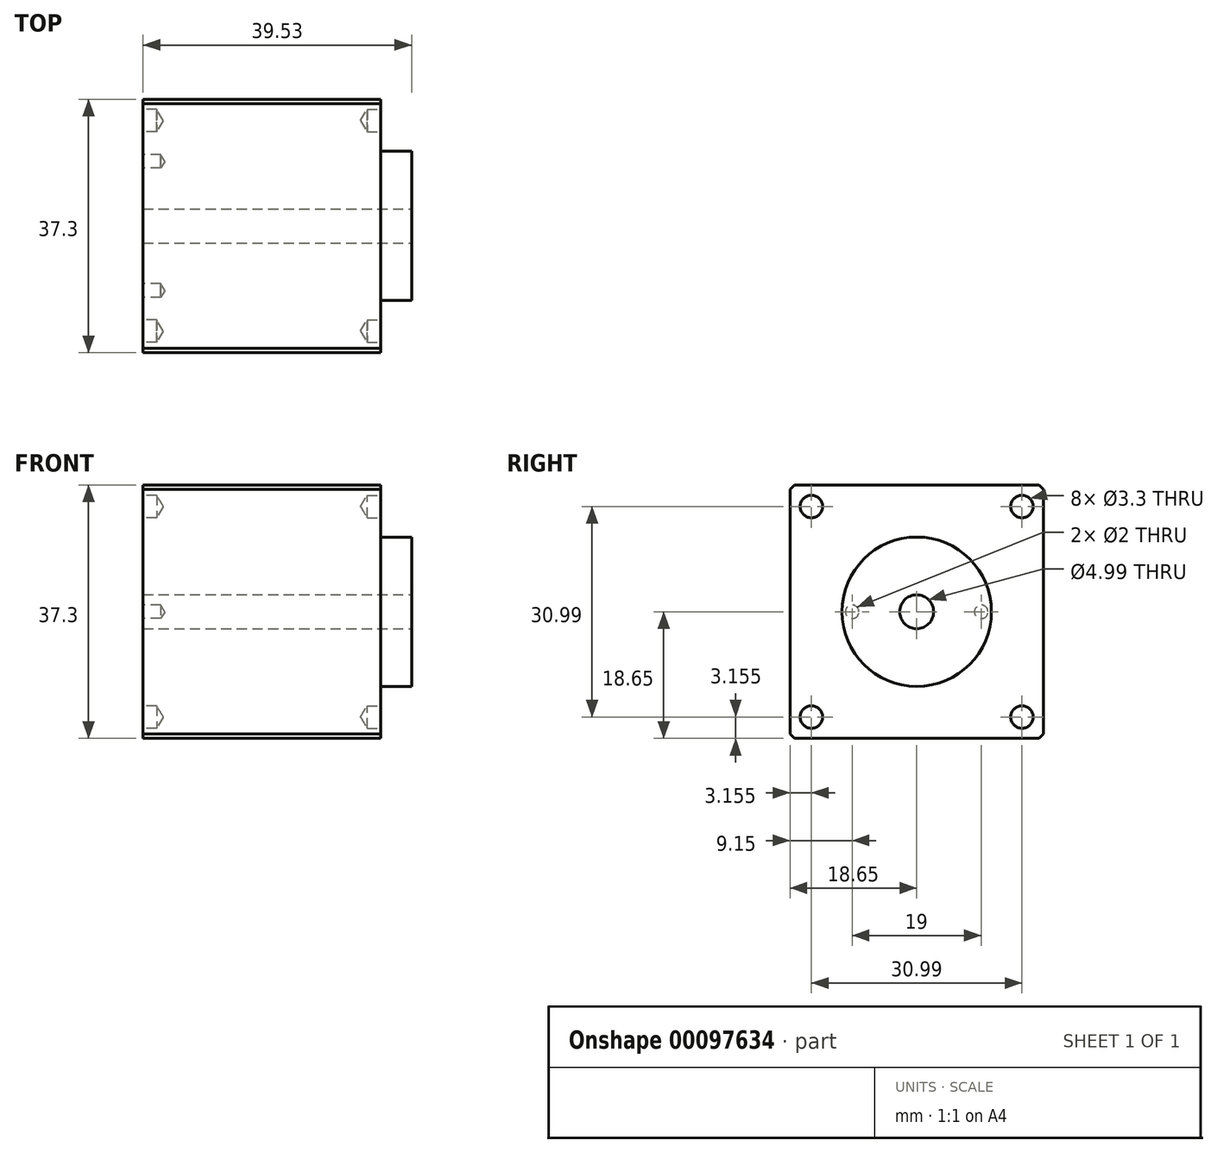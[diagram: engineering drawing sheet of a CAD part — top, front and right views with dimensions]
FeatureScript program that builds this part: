
annotation { "Feature Type Name" : "Feature", "Feature Type Description" : "" }
export const myFeature = defineFeature(function(context is Context, id is Id, definition is map)
    precondition{}
    {
        {
            var Q0;
            Q0=qCreatedBy(makeId("Right.planeOp"),FACE);
            var sketch = newSketch(context, id + "F0", { "sketchPlane" : qUnion([Q0])});
            skLineSegment(sketch, "E0.bottom", {"start": v(18, -18.65) * mm, "end": v(-18, -18.65) * mm});
            skLineSegment(sketch, "E0.top", {"start": v(18, 18.65) * mm, "end": v(-18, 18.65) * mm});
            skLineSegment(sketch, "E0.left", {"start": v(18.65, -18) * mm, "end": v(18.65, 18) * mm});
            skLineSegment(sketch, "E0.right", {"start": v(-18.65, -18) * mm, "end": v(-18.65, 18) * mm});
            skPoint(sketch, "E0.middle", {"position": v(0, 0) * mm});
            skLineSegment(sketch, "E1", {"start": v(-18, 18.65) * mm, "end": v(-18.65, 18) * mm});
            skLineSegment(sketch, "E2.MirrorCS", {"start": v(18, 18.65) * mm, "end": v(18.65, 18) * mm});
            skLineSegment(sketch, "E3.MirrorCS", {"start": v(-18, -18.65) * mm, "end": v(-18.65, -18) * mm});
            skLineSegment(sketch, "E4.MirrorCS", {"start": v(18, -18.65) * mm, "end": v(18.65, -18) * mm});
            skCircle(sketch, "E5", {"center": v(0, 0) * mm, "radius": 11 * mm});
            skCircle(sketch, "E6", {"center": v(0, 0) * mm, "radius": 2.5 * mm});
            skPoint(sketch, "E7", {"position": v(-15.5, 15.5) * mm});
            skPoint(sketch, "E8.MirrorP", {"position": v(15.5, 15.5) * mm});
            skPoint(sketch, "E9.MirrorP", {"position": v(-15.5, -15.5) * mm});
            skPoint(sketch, "E10.MirrorP", {"position": v(15.5, -15.5) * mm});
            skPoint(sketch, "E11", {"position": v(-9.5, 0) * mm});
            skPoint(sketch, "E12.MirrorP", {"position": v(9.5, 0) * mm});
            skSolve(sketch);
        }
        {
            var Q0;
            Q0=makeQuery(id+"F0.imprint","IMPRINT",FACE,{"disambiguationData":[TD([[makeQuery(id+"F0.imprint","IMPRINT",EDGE,{"derivedFrom":sQuery(id+"F0.wireOp",EDGE,"E0.bottom")}),-1.0]])]});
            extrude(context, id + "F1", {"entities" : qUnion([Q0]), "endBound" : BoundingType.SYMMETRIC, "depth" : 35 * mm});
        }
        {
            var Q0;
            Q0=makeQuery(id+"F0.imprint","IMPRINT",FACE,{"disambiguationData":[TD([[makeQuery(id+"F0.imprint","IMPRINT",EDGE,{"derivedFrom":sQuery(id+"F0.wireOp",EDGE,"E5")}),1.0]])]});
            var Q1;
            Q1=makeQuery(id+"F1.opExtrude","CAP_FACE",FACE,{"disambiguationData":[OSD([sQuery(id+"F0.wireOp",EDGE,"E0.bottom"),sQuery(id+"F0.wireOp",EDGE,"E0.top"),sQuery(id+"F0.wireOp",EDGE,"E0.left"),sQuery(id+"F0.wireOp",EDGE,"E0.right"),sQuery(id+"F0.wireOp",EDGE,"E1"),sQuery(id+"F0.wireOp",EDGE,"E2.MirrorCS"),sQuery(id+"F0.wireOp",EDGE,"E3.MirrorCS"),sQuery(id+"F0.wireOp",EDGE,"E4.MirrorCS"),sQuery(id+"F0.wireOp",EDGE,"E5")])],"isStart":true});
            extrude(context, id + "F2", {"entities" : qUnion([Q0]), "operationType" : NewBodyOperationType.ADD, "endBound" : BoundingType.UP_TO_SURFACE, "oppositeDirection" : true, "endBoundEntityFace" : qUnion([Q1]), "depth" : 15 * mm});
        }
        {
            var Q0;
            Q0=makeQuery(id+"F0.imprint","IMPRINT",FACE,{"disambiguationData":[TD([[makeQuery(id+"F0.imprint","IMPRINT",EDGE,{"derivedFrom":sQuery(id+"F0.wireOp",EDGE,"E5")}),1.0]])]});
            extrude(context, id + "F3", {"entities" : qUnion([Q0]), "operationType" : NewBodyOperationType.ADD, "depth" : 22.03 * mm});
        }
        {
            var Q0;
            Q0=makeQuery(id+"F1.opExtrude","CAP_FACE",FACE,{"disambiguationData":[OSD([sQuery(id+"F0.wireOp",EDGE,"E0.bottom"),sQuery(id+"F0.wireOp",EDGE,"E0.top"),sQuery(id+"F0.wireOp",EDGE,"E0.left"),sQuery(id+"F0.wireOp",EDGE,"E0.right"),sQuery(id+"F0.wireOp",EDGE,"E1"),sQuery(id+"F0.wireOp",EDGE,"E2.MirrorCS"),sQuery(id+"F0.wireOp",EDGE,"E3.MirrorCS"),sQuery(id+"F0.wireOp",EDGE,"E4.MirrorCS"),sQuery(id+"F0.wireOp",EDGE,"E5")])],"isStart":false});
            var sketch = newSketch(context, id + "F4", { "sketchPlane" : qUnion([Q0])});
            skPoint(sketch, "E13", {"position": v(-15.5, 15.5) * mm});
            skPoint(sketch, "E14", {"position": v(-15.5, -15.5) * mm});
            skPoint(sketch, "E15.MirrorP", {"position": v(15.5, 15.5) * mm});
            skPoint(sketch, "E16.MirrorP", {"position": v(15.5, -15.5) * mm});
            skSolve(sketch);
        }
        {
            var Q0;
            {var subQ0=sQuery(id+"F0.wireOp",EDGE,"E5");Q0=makeQuery(id+"F2.boolean.opBoolean","MERGE",FACE,{"derivedFrom":[makeQuery(id+"F1.opExtrude","CAP_FACE",FACE,{"disambiguationData":[OSD([sQuery(id+"F0.wireOp",EDGE,"E0.bottom"),sQuery(id+"F0.wireOp",EDGE,"E0.top"),sQuery(id+"F0.wireOp",EDGE,"E0.left"),sQuery(id+"F0.wireOp",EDGE,"E0.right"),sQuery(id+"F0.wireOp",EDGE,"E1"),sQuery(id+"F0.wireOp",EDGE,"E2.MirrorCS"),sQuery(id+"F0.wireOp",EDGE,"E3.MirrorCS"),sQuery(id+"F0.wireOp",EDGE,"E4.MirrorCS"),subQ0])],"isStart":true}),makeQuery(id+"F2.opExtrude","CAP_FACE",FACE,{"disambiguationData":[OSD([subQ0,sQuery(id+"F0.wireOp",EDGE,"E6")])],"isStart":false})]});}
            var sketch = newSketch(context, id + "F5", { "sketchPlane" : qUnion([Q0])});
            skPoint(sketch, "E17", {"position": v(-15.5, 15.5) * mm});
            skPoint(sketch, "E18", {"position": v(-15.5, -15.5) * mm});
            skPoint(sketch, "E19", {"position": v(-9.5, 0) * mm});
            skPoint(sketch, "E20.MirrorP", {"position": v(15.5, 15.5) * mm});
            skPoint(sketch, "E21.MirrorP", {"position": v(9.5, 0) * mm});
            skPoint(sketch, "E22.MirrorP", {"position": v(15.5, -15.5) * mm});
            skSolve(sketch);
        }
        {
            var Q0;
            Q0=sQuery(id+"F4.wireOp",VERTEX,"E15.MirrorP");
            var Q1;
            Q1=sQuery(id+"F4.wireOp",VERTEX,"E13");
            var Q2;
            Q2=sQuery(id+"F4.wireOp",VERTEX,"E16.MirrorP");
            var Q3;
            Q3=sQuery(id+"F4.wireOp",VERTEX,"E14");
            var Q4;
            Q4=makeQuery(id+"F1.opExtrude","SWEPT_BODY",BODY,{"disambiguationData":[OSD([sQuery(id+"F0.wireOp",EDGE,"E0.bottom"),sQuery(id+"F0.wireOp",EDGE,"E0.top"),sQuery(id+"F0.wireOp",EDGE,"E0.left"),sQuery(id+"F0.wireOp",EDGE,"E0.right"),sQuery(id+"F0.wireOp",EDGE,"E1"),sQuery(id+"F0.wireOp",EDGE,"E2.MirrorCS"),sQuery(id+"F0.wireOp",EDGE,"E3.MirrorCS"),sQuery(id+"F0.wireOp",EDGE,"E4.MirrorCS"),sQuery(id+"F0.wireOp",EDGE,"E5")])]});
            hole(context, id + "F6", {"style" : HoleStyle.SIMPLE, "endStyle" : HoleEndStyle.BLIND, "standardTappedOrClearance" : lookupTablePath({ "standard" : "ISO", "fit" : "Normal", "size" : "M3", "type" : "Clearance" }), "standardBlindInLast" : lookupTablePath({ "fit" : "Standard", "standard" : "ISO", "size" : "M3", "type" : "Clearance" }), "holeDiameter" : 3.3 * mm, "holeDepth" : 2 * mm, "locations" : qUnion([Q0, Q1, Q2, Q3]), "scope" : qUnion([Q4])});
        }
        {
            var Q0;
            Q0=sQuery(id+"F5.wireOp",VERTEX,"E17");
            var Q1;
            Q1=sQuery(id+"F5.wireOp",VERTEX,"E18");
            var Q2;
            Q2=sQuery(id+"F5.wireOp",VERTEX,"E22.MirrorP");
            var Q3;
            Q3=sQuery(id+"F5.wireOp",VERTEX,"E20.MirrorP");
            var Q4;
            Q4=makeQuery(id+"F1.opExtrude","SWEPT_BODY",BODY,{"disambiguationData":[OSD([sQuery(id+"F0.wireOp",EDGE,"E0.bottom"),sQuery(id+"F0.wireOp",EDGE,"E0.top"),sQuery(id+"F0.wireOp",EDGE,"E0.left"),sQuery(id+"F0.wireOp",EDGE,"E0.right"),sQuery(id+"F0.wireOp",EDGE,"E1"),sQuery(id+"F0.wireOp",EDGE,"E2.MirrorCS"),sQuery(id+"F0.wireOp",EDGE,"E3.MirrorCS"),sQuery(id+"F0.wireOp",EDGE,"E4.MirrorCS"),sQuery(id+"F0.wireOp",EDGE,"E5")])]});
            hole(context, id + "F7", {"style" : HoleStyle.SIMPLE, "endStyle" : HoleEndStyle.BLIND, "standardTappedOrClearance" : lookupTablePath({ "standard" : "ISO", "fit" : "Normal", "size" : "M3", "type" : "Clearance" }), "standardBlindInLast" : lookupTablePath({ "fit" : "Standard", "standard" : "ISO", "size" : "M3", "type" : "Clearance" }), "holeDiameter" : 3.3 * mm, "holeDepth" : 2 * mm, "locations" : qUnion([Q0, Q1, Q2, Q3]), "scope" : qUnion([Q4])});
        }
        {
            var Q0;
            Q0=sQuery(id+"F5.wireOp",VERTEX,"E19");
            var Q1;
            Q1=sQuery(id+"F5.wireOp",VERTEX,"E21.MirrorP");
            var Q2;
            Q2=makeQuery(id+"F1.opExtrude","SWEPT_BODY",BODY,{"disambiguationData":[OSD([sQuery(id+"F0.wireOp",EDGE,"E0.bottom"),sQuery(id+"F0.wireOp",EDGE,"E0.top"),sQuery(id+"F0.wireOp",EDGE,"E0.left"),sQuery(id+"F0.wireOp",EDGE,"E0.right"),sQuery(id+"F0.wireOp",EDGE,"E1"),sQuery(id+"F0.wireOp",EDGE,"E2.MirrorCS"),sQuery(id+"F0.wireOp",EDGE,"E3.MirrorCS"),sQuery(id+"F0.wireOp",EDGE,"E4.MirrorCS"),sQuery(id+"F0.wireOp",EDGE,"E5")])]});
            hole(context, id + "F8", {"style" : HoleStyle.SIMPLE, "endStyle" : HoleEndStyle.BLIND, "holeDiameter" : 2 * mm, "holeDepth" : 2.6 * mm, "locations" : qUnion([Q0, Q1]), "scope" : qUnion([Q2])});
        }
    });
